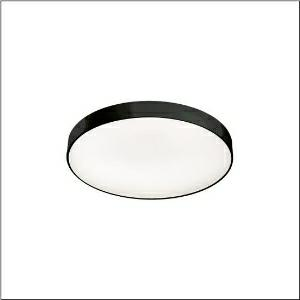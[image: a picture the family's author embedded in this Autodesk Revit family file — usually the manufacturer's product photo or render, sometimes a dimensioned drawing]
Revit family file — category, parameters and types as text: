
# Revit family: round_21_m_51mr36nd0421b
name_source: partatom
category: Lighting Fixtures
units: mm (PartAtom-declared; Revit-internal decimal feet)

## family parameters
Cut with Voids When Loaded = No
Host = Face
Light Source = No
Part Type = Normal
Room Calculation Point = No
Round Connector Dimension = Use Diameter
Shared = No

## types (1)
- Round 21 M (1 x LED, 7470 lm, 54.6 W, 4000K)
    Apparent Load = 55 VA
    CIE Flux Codes = 66 90 98 84 100
    Color Rendering = 80
    Color Temperature = 4000K
    Default Elevation = 1800 mm
    Description = Round 21 M, wall and ceiling luminaire, primary optical cover: micro prismatic cover, of PMMA, transparent, CAT 2 (L<= 3000cd/m²), light emission: direct/indirect distribution, primary light characteristic: symmetric, installation type: surface-mounted, suspended mounting, LED, rated luminous flux: 7.470lm, luminous efficacy: 137lm/W, light colour: 840, colour temperature: 4000K, control gear: DALI 2, with terminal, 5-pole, mains connection: 230V, AC, 50/60Hz, rated input power: 54.6W, housing, of aluminium, coated, black, diameter: 600mm, height: 62mm, protection rating (complete): IP40, insulation class (complete): insulation class I (protective earthing), certification: CE, impact resistance: IK04, permissible operating ambient temperature: -10..+35°C, packaging unit: 1 piece
    Height = 87 mm
    Lamp = 1 x LED
    Lamp Light Flux = 7470 lm
    Lamp Power = 54.6 W
    Lamp count = 1
    Length = 600 mm
    Luminous efficacy = 137 lm/W
    Manufacturer = Siteco
    ModVariant = No
    Model = 51MR36ND0421B
    Mounting Place = Ceiling
    Mounting Type = Surface mounted
    Number of Poles = 1
    OnlyDefault = Yes
    Power Factor = 1
    Product Name = Round 21 M
    Product group = wall and ceiling luminaire
    ProductGroupID = 304
    Protection Class = Protection class I
    Protection Degree = IP 40
    RLX_Detail_Level = 1
    RLX_Emergency_Light_Flux = 0 lm
    RLX_Emergency_Type = 0
    RLX_Emergency_Type_DB = No
    RlxData = <blob elided: 21941 chars, md5=a030c245>
    Socket = socket
    Standby Power = 0 W
    System Light Flux = 7470 lm
    System Power = 55 W
    Type Comments = Product without accessories
    Type Image = l_1258305.jpg
    URL = http://relux.com
    VarID = ---
    Voltage = 0 V
    Weight = 0.00 kg
    Width = 0 mm  [stored 0 ft]

note: [stored X ft] marks values corroborated as IEEE doubles in the binary element streams (Revit-internal decimal feet)

## geometry (parser evidence)
native form markers: Blend x4, Sweep x13
no freeform markers — native parametric forms only
